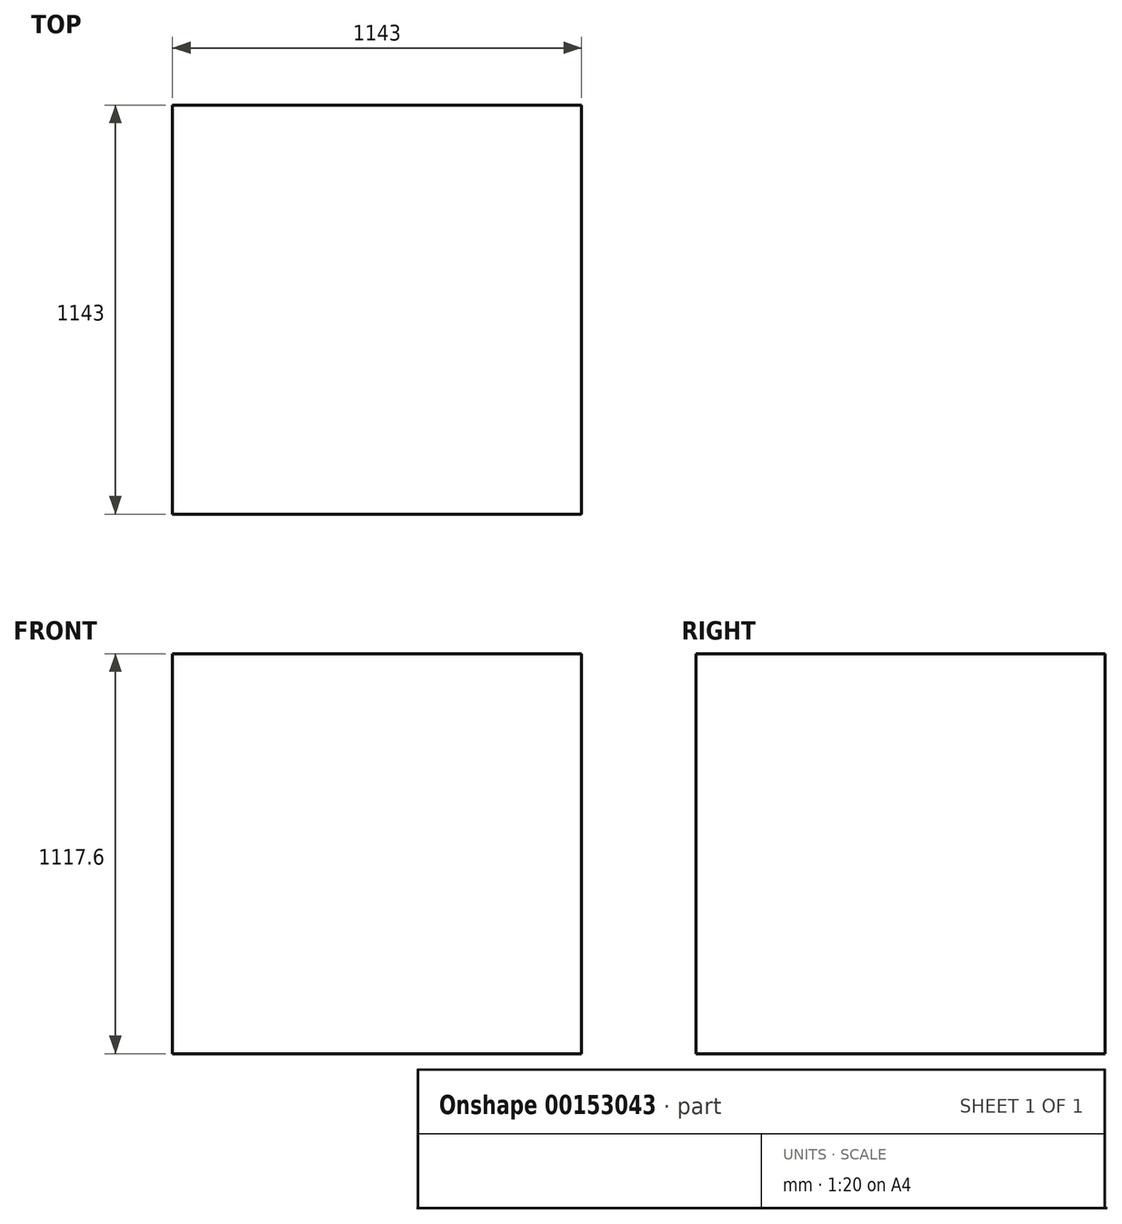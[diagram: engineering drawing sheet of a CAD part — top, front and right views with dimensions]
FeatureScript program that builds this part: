
annotation { "Feature Type Name" : "Feature", "Feature Type Description" : "" }
export const myFeature = defineFeature(function(context is Context, id is Id, definition is map)
    precondition{}
    {
        {
            var Q0;
            Q0=qCreatedBy(makeId("Top.planeOp"),FACE);
            var sketch = newSketch(context, id + "F0", { "sketchPlane" : qUnion([Q0])});
            skLineSegment(sketch, "E0.bottom", {"start": v(0, 0) * mm, "end": v(-1143, 0) * mm});
            skLineSegment(sketch, "E0.top", {"start": v(0, -1143) * mm, "end": v(-1143, -1143) * mm});
            skLineSegment(sketch, "E0.left", {"start": v(0, 0) * mm, "end": v(0, -1143) * mm});
            skLineSegment(sketch, "E0.right", {"start": v(-1143, 0) * mm, "end": v(-1143, -1143) * mm});
            skSolve(sketch);
        }
        {
            var Q0;
            Q0 = qSketchRegion(id + "F0", true);
            extrude(context, id + "F1", {"entities" : qUnion([Q0]), "depth" : 1117.6 * mm});
        }
    });
